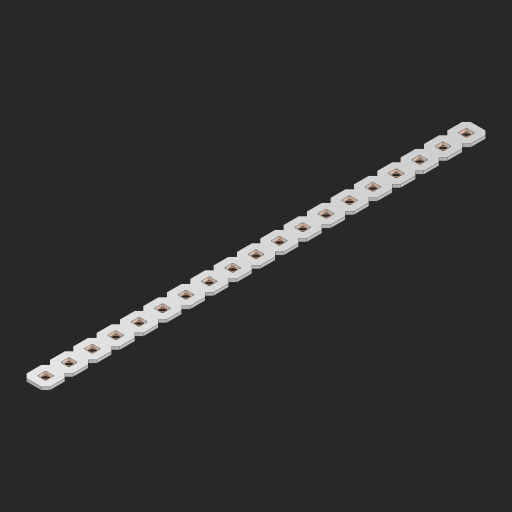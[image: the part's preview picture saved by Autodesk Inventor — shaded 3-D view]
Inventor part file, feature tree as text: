
AUTODESK INVENTOR PART (.ipt)
format: ipt  version: 2023 (Build 270158000, 158)  size: 477,184 bytes
history: native  units: in
note: dims shown in document units (in); Inventor stores cm internally (conversion verified against a paired STEP export)
features: other x20, extrude x18, sketch x2, pattern_linear x1
ambient origin geometry x8: Origin, YZ Plane, XZ Plane, XY Plane, X Axis, Y Axis, Z Axis, Center Point
bodies: Solid1 (feature_tree), Body (feature_tree)
feature tree (41):
  pattern_linear  "Rectangular Pattern1"  Spacing1=0.09in  [1 undecoded]
  sketch  "Sketch1"  dims[d1=0.5in]
  sketch  "Sketch2"  dims[d2=0.182in d3=0.09in d4=0.09in d5=0.09in d6=0.09in d7=0.09in d8=0.09in d9=0.09in d10=0.09in d11=0.02in d13=0.0in d14=0.172in d15=0.0625in d16=0.0in d19=0.5in d22=0.5in]
  other  "Srf1"
  other  "Srf126"
  other  "Srf127"
  other  "Srf128"
  other  "Srf129"
  other  "Srf130"
  other  "Srf131"
  other  "Srf250"
  other  "Srf251"
  other  "Srf252"
  other  "Srf253"
  other  "Srf254"
  other  "Srf255"
  other  "Srf256"
  other  "Srf257"
  other  "Srf258"
  other  "Srf259"
  other  "Srf260"
  other  "Srf261"
  other  "Circle"
  extrude  "ExtrusionSrf126"  Depth=0.09in
  extrude  "ExtrusionSrf127"  Depth=0.09in
  extrude  "ExtrusionSrf128"  Depth=0.09in
  extrude  "ExtrusionSrf129"  Depth=0.09in
  extrude  "ExtrusionSrf130"  Depth=0.09in
  extrude  "ExtrusionSrf131"  Depth=0.09in
  extrude  "ExtrusionSrf250"  Depth=0.09in
  extrude  "ExtrusionSrf251"  Depth=0.02in
  extrude  "ExtrusionSrf252"  TaperAngle=0.0deg  [1 undecoded]
  extrude  "ExtrusionSrf253"  Depth=0.5in
  extrude  "ExtrusionSrf254"  Depth=0.0625in TaperAngle=0.0deg
  extrude  "ExtrusionSrf255"  Depth=0.5in
  extrude  "ExtrusionSrf256"  Depth=0.5in
  extrude  "ExtrusionSrf257"  [1 undecoded]
  extrude  "ExtrusionSrf258"  [1 undecoded]
  extrude  "ExtrusionSrf259"  [1 undecoded]
  extrude  "ExtrusionSrf260"  [1 undecoded]
  extrude  "ExtrusionSrf261"  [1 undecoded]
note: 7 required parameter values undecoded (feature->parameter linkage not recoverable at this tier; creation-order binding heuristic only, values carry confidence <= 0.55)
